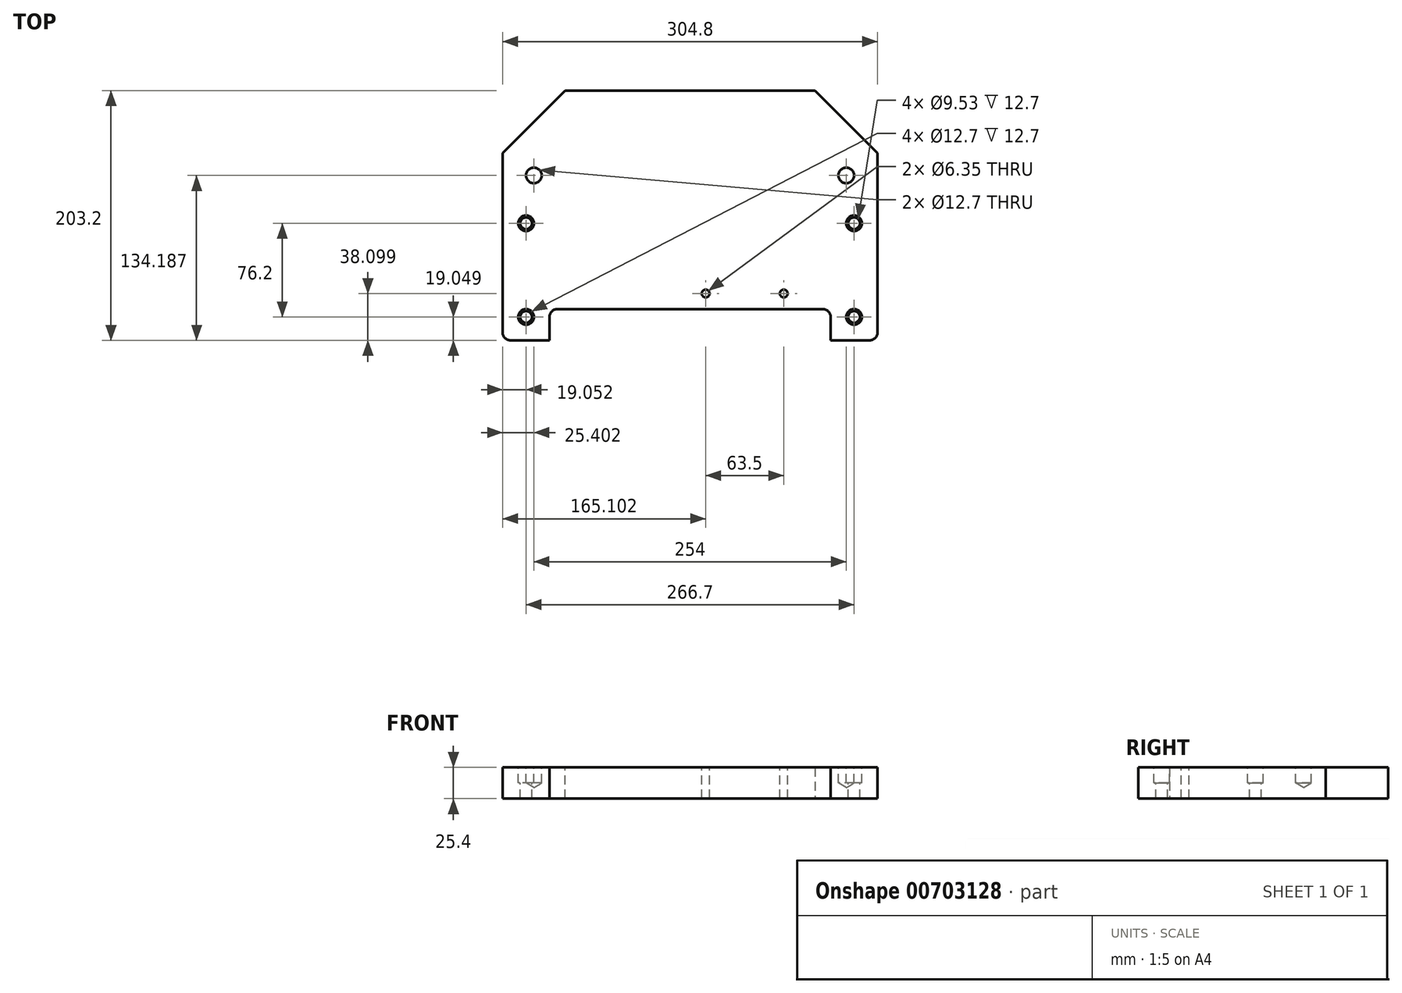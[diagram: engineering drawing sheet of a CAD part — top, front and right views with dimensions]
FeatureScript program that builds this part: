
annotation { "Feature Type Name" : "Feature", "Feature Type Description" : "" }
export const myFeature = defineFeature(function(context is Context, id is Id, definition is map)
    precondition{}
    {
        {
            var Q0;
            Q0=qCreatedBy(makeId("Top.planeOp"),FACE);
            var sketch = newSketch(context, id + "F0", { "sketchPlane" : qUnion([Q0])});
            skLineSegment(sketch, "E0.bottom", {"start": v(-151.45, -100.14) * mm, "end": v(153.35, -100.14) * mm});
            skLineSegment(sketch, "E0.top", {"start": v(-151.45, 103.06) * mm, "end": v(153.35, 103.06) * mm});
            skLineSegment(sketch, "E0.left", {"start": v(-151.45, -100.14) * mm, "end": v(-151.45, 103.06) * mm});
            skLineSegment(sketch, "E0.right", {"start": v(153.35, -100.14) * mm, "end": v(153.35, 103.06) * mm});
            skSolve(sketch);
        }
        {
            var Q0;
            Q0=makeQuery(id+"F0.imprint","IMPRINT",FACE,{"disambiguationData":[TD([[makeQuery(id+"F0.imprint","IMPRINT",EDGE,{"derivedFrom":sQuery(id+"F0.wireOp",EDGE,"E0.bottom")}),1.0]])]});
            extrude(context, id + "F1", {"entities" : qUnion([Q0]), "depth" : 25.4 * mm, "offsetDistance" : 25.4 * mm});
        }
        {
            var Q0;
            Q0=makeQuery(id+"F1.opExtrude","SWEPT_FACE",FACE,{"disambiguationData":[OSD([sQuery(id+"F0.wireOp",EDGE,"E0.bottom")])]});
            var sketch = newSketch(context, id + "F2", { "sketchPlane" : qUnion([Q0])});
            skSolve(sketch);
        }
        {
            var Q0;
            Q0=makeQuery(id+"F1.opExtrude","SWEPT_EDGE",EDGE,{"disambiguationData":[OSD([sQuery(id+"F0.wireOp",EDGE,"E0.top"),sQuery(id+"F0.wireOp",EDGE,"E0.left")])]});
            var Q1;
            Q1=makeQuery(id+"F1.opExtrude","SWEPT_EDGE",EDGE,{"disambiguationData":[OSD([sQuery(id+"F0.wireOp",EDGE,"E0.top"),sQuery(id+"F0.wireOp",EDGE,"E0.right")])]});
            chamfer(context, id + "F3", {"entities" : qUnion([Q0, Q1]), "width" : 50.8 * mm, "tangentPropagation" : true});
        }
        {
            var Q0;
            {var subQ0=sQuery(id+"F0.wireOp",EDGE,"E0.bottom");Q0=makeQuery(id+"F2.imprint","IMPRINT",FACE,{"disambiguationData":[TD([[makeQuery(id+"F2.imprint","IMPRINT",EDGE,{"derivedFrom":makeQuery(id+"F1.opExtrude","CAP_EDGE",EDGE,{"disambiguationData":[OSD([subQ0])],"isStart":true})}),1.0]])]});}
            var sketch = newSketch(context, id + "F4", { "sketchPlane" : qUnion([Q0])});
            skLineSegment(sketch, "E1.0", {"start": v(-113.35, 25.4) * mm, "end": v(115.25, 25.4) * mm});
            skLineSegment(sketch, "E2.0", {"start": v(-113.35, 0) * mm, "end": v(115.25, 0) * mm});
            skLineSegment(sketch, "E3.left", {"start": v(-113.35, 25.4) * mm, "end": v(-113.35, 0) * mm});
            skLineSegment(sketch, "E3.right", {"start": v(115.25, 25.4) * mm, "end": v(115.25, 0) * mm});
            skPoint(sketch, "E4.orphan", {"position": v(-151.45, 25.4) * mm});
            skPoint(sketch, "E5.orphan", {"position": v(-151.45, 0) * mm});
            skPoint(sketch, "E6.orphan", {"position": v(153.35, 25.4) * mm});
            skPoint(sketch, "E7.orphan", {"position": v(153.35, 0) * mm});
            skSolve(sketch);
        }
        {
            var Q0;
            Q0=qSketchRegion(id+"F4",true);
            extrude(context, id + "F5", {"entities" : qUnion([Q0]), "operationType" : NewBodyOperationType.REMOVE, "oppositeDirection" : true, "depth" : 25.4 * mm, "offsetDistance" : 25.4 * mm});
        }
        {
            var Q0;
            Q0=makeQuery(id+"F5.boolean.opBoolean","COPY",EDGE,{"derivedFrom":makeQuery(id+"F5.opExtrude","CAP_EDGE",EDGE,{"disambiguationData":[OSD([sQuery(id+"F4.wireOp",EDGE,"E3.left")])],"isStart":true})});
            var Q1;
            Q1=makeQuery(id+"F5.boolean.opBoolean","COPY",EDGE,{"derivedFrom":makeQuery(id+"F5.opExtrude","CAP_EDGE",EDGE,{"disambiguationData":[OSD([sQuery(id+"F4.wireOp",EDGE,"E3.left")])],"isStart":false})});
            var Q2;
            Q2=makeQuery(id+"F5.boolean.opBoolean","COPY",EDGE,{"derivedFrom":makeQuery(id+"F5.opExtrude","CAP_EDGE",EDGE,{"disambiguationData":[OSD([sQuery(id+"F4.wireOp",EDGE,"E3.right")])],"isStart":false})});
            var Q3;
            Q3=makeQuery(id+"F5.boolean.opBoolean","COPY",EDGE,{"derivedFrom":makeQuery(id+"F5.opExtrude","CAP_EDGE",EDGE,{"disambiguationData":[OSD([sQuery(id+"F4.wireOp",EDGE,"E3.right")])],"isStart":true})});
            var Q4;
            Q4=makeQuery(id+"F1.opExtrude","SWEPT_EDGE",EDGE,{"disambiguationData":[OSD([sQuery(id+"F0.wireOp",EDGE,"E0.bottom"),sQuery(id+"F0.wireOp",EDGE,"E0.right")])]});
            var Q5;
            Q5=makeQuery(id+"F1.opExtrude","SWEPT_EDGE",EDGE,{"disambiguationData":[OSD([sQuery(id+"F0.wireOp",EDGE,"E0.bottom"),sQuery(id+"F0.wireOp",EDGE,"E0.left")])]});
            fillet(context, id + "F6", {"entities" : qUnion([Q0, Q1, Q2, Q3, Q4, Q5]), "radius" : 6.35 * mm, "tangentPropagation" : true, "allowEdgeOverflow" : false});
        }
        {
            var Q0;
            Q0=makeQuery(id+"F1.opExtrude","CAP_FACE",FACE,{"disambiguationData":[OSD([sQuery(id+"F0.wireOp",EDGE,"E0.bottom"),sQuery(id+"F0.wireOp",EDGE,"E0.top"),sQuery(id+"F0.wireOp",EDGE,"E0.left"),sQuery(id+"F0.wireOp",EDGE,"E0.right")])],"isStart":false});
            var sketch = newSketch(context, id + "F7", { "sketchPlane" : qUnion([Q0])});
            skPoint(sketch, "E8", {"position": v(-132.4, -81.1) * mm});
            skPoint(sketch, "E9", {"position": v(134.3, -81.1) * mm});
            skPoint(sketch, "E10", {"position": v(-132.4, -4.9) * mm});
            skPoint(sketch, "E11", {"position": v(134.3, -4.9) * mm});
            skSolve(sketch);
        }
        {
            var Q0;
            Q0=sQuery(id+"F7.wireOp",VERTEX,"E8");
            var Q1;
            Q1=sQuery(id+"F7.wireOp",VERTEX,"E10");
            var Q2;
            Q2=sQuery(id+"F7.wireOp",VERTEX,"E11");
            var Q3;
            Q3=sQuery(id+"F7.wireOp",VERTEX,"E9");
            var Q4;
            Q4=makeQuery(id+"F1.opExtrude","SWEPT_BODY",BODY,{"disambiguationData":[OSD([sQuery(id+"F0.wireOp",EDGE,"E0.bottom"),sQuery(id+"F0.wireOp",EDGE,"E0.top"),sQuery(id+"F0.wireOp",EDGE,"E0.left"),sQuery(id+"F0.wireOp",EDGE,"E0.right")])]});
            hole(context, id + "F8", {"style" : HoleStyle.C_BORE, "endStyle" : HoleEndStyle.THROUGH, "holeDiameter" : 9.52 * mm, "cBoreDiameter" : 12.7 * mm, "cBoreDepth" : 12.7 * mm, "majorDiameter" : 6.35 * mm, "isTappedThrough" : true, "tappedDepth" : 12.7 * mm, "tapClearance" : 3, "locations" : qUnion([Q0, Q1, Q2, Q3]), "scope" : qUnion([Q4])});
        }
        {
            var Q0;
            Q0=makeQuery(id+"F1.opExtrude","CAP_FACE",FACE,{"disambiguationData":[OSD([sQuery(id+"F0.wireOp",EDGE,"E0.bottom"),sQuery(id+"F0.wireOp",EDGE,"E0.top"),sQuery(id+"F0.wireOp",EDGE,"E0.left"),sQuery(id+"F0.wireOp",EDGE,"E0.right")])],"isStart":false});
            var sketch = newSketch(context, id + "F9", { "sketchPlane" : qUnion([Q0])});
            skPoint(sketch, "E12", {"position": v(13.65, -62.04) * mm});
            skLineSegment(sketch, "E13.0", {"start": v(-145.1, -100.14) * mm, "end": v(-119.7, -100.14) * mm});
            skPoint(sketch, "E14.1.0.0", {"position": v(77.15, -62.04) * mm});
            skLineSegment(sketch, "E14.direction1", {"start": v(13.65, -62.04) * mm, "end": v(77.15, -62.04) * mm, "construction": true});
            skSolve(sketch);
        }
        {
            var Q0;
            Q0=sQuery(id+"F9.wireOp",VERTEX,"E12");
            var Q1;
            Q1=sQuery(id+"F9.wireOp",VERTEX,"E14.1.0.0");
            var Q2;
            Q2=makeQuery(id+"F1.opExtrude","SWEPT_BODY",BODY,{"disambiguationData":[OSD([sQuery(id+"F0.wireOp",EDGE,"E0.bottom"),sQuery(id+"F0.wireOp",EDGE,"E0.top"),sQuery(id+"F0.wireOp",EDGE,"E0.left"),sQuery(id+"F0.wireOp",EDGE,"E0.right")])]});
            hole(context, id + "F10", {"style" : HoleStyle.SIMPLE, "endStyle" : HoleEndStyle.THROUGH, "holeDiameter" : 6.35 * mm, "majorDiameter" : 6.35 * mm, "isTappedThrough" : true, "tappedDepth" : 12.7 * mm, "tapClearance" : 3, "locations" : qUnion([Q0, Q1]), "scope" : qUnion([Q2])});
        }
        {
            var Q0;
            Q0=makeQuery(id+"F1.opExtrude","CAP_FACE",FACE,{"disambiguationData":[OSD([sQuery(id+"F0.wireOp",EDGE,"E0.bottom"),sQuery(id+"F0.wireOp",EDGE,"E0.top"),sQuery(id+"F0.wireOp",EDGE,"E0.left"),sQuery(id+"F0.wireOp",EDGE,"E0.right")])],"isStart":false});
            var sketch = newSketch(context, id + "F11", { "sketchPlane" : qUnion([Q0])});
            skPoint(sketch, "E15", {"position": v(-126.05, 34.05) * mm});
            skPoint(sketch, "E16.1.0.0", {"position": v(127.95, 34.05) * mm});
            skLineSegment(sketch, "E16.direction1", {"start": v(-126.05, 34.05) * mm, "end": v(127.95, 34.05) * mm, "construction": true});
            skSolve(sketch);
        }
        {
            var Q0;
            Q0=sQuery(id+"F11.wireOp",VERTEX,"E15");
            var Q1;
            Q1=sQuery(id+"F11.wireOp",VERTEX,"E16.1.0.0");
            var Q2;
            Q2=makeQuery(id+"F1.opExtrude","SWEPT_BODY",BODY,{"disambiguationData":[OSD([sQuery(id+"F0.wireOp",EDGE,"E0.bottom"),sQuery(id+"F0.wireOp",EDGE,"E0.top"),sQuery(id+"F0.wireOp",EDGE,"E0.left"),sQuery(id+"F0.wireOp",EDGE,"E0.right")])]});
            hole(context, id + "F12", {"style" : HoleStyle.SIMPLE, "endStyle" : HoleEndStyle.BLIND, "holeDiameter" : 12.7 * mm, "majorDiameter" : 6.35 * mm, "holeDepth" : 12.7 * mm, "isTappedThrough" : true, "tappedDepth" : 12.7 * mm, "tapClearance" : 3, "locations" : qUnion([Q0, Q1]), "scope" : qUnion([Q2])});
        }
    });
